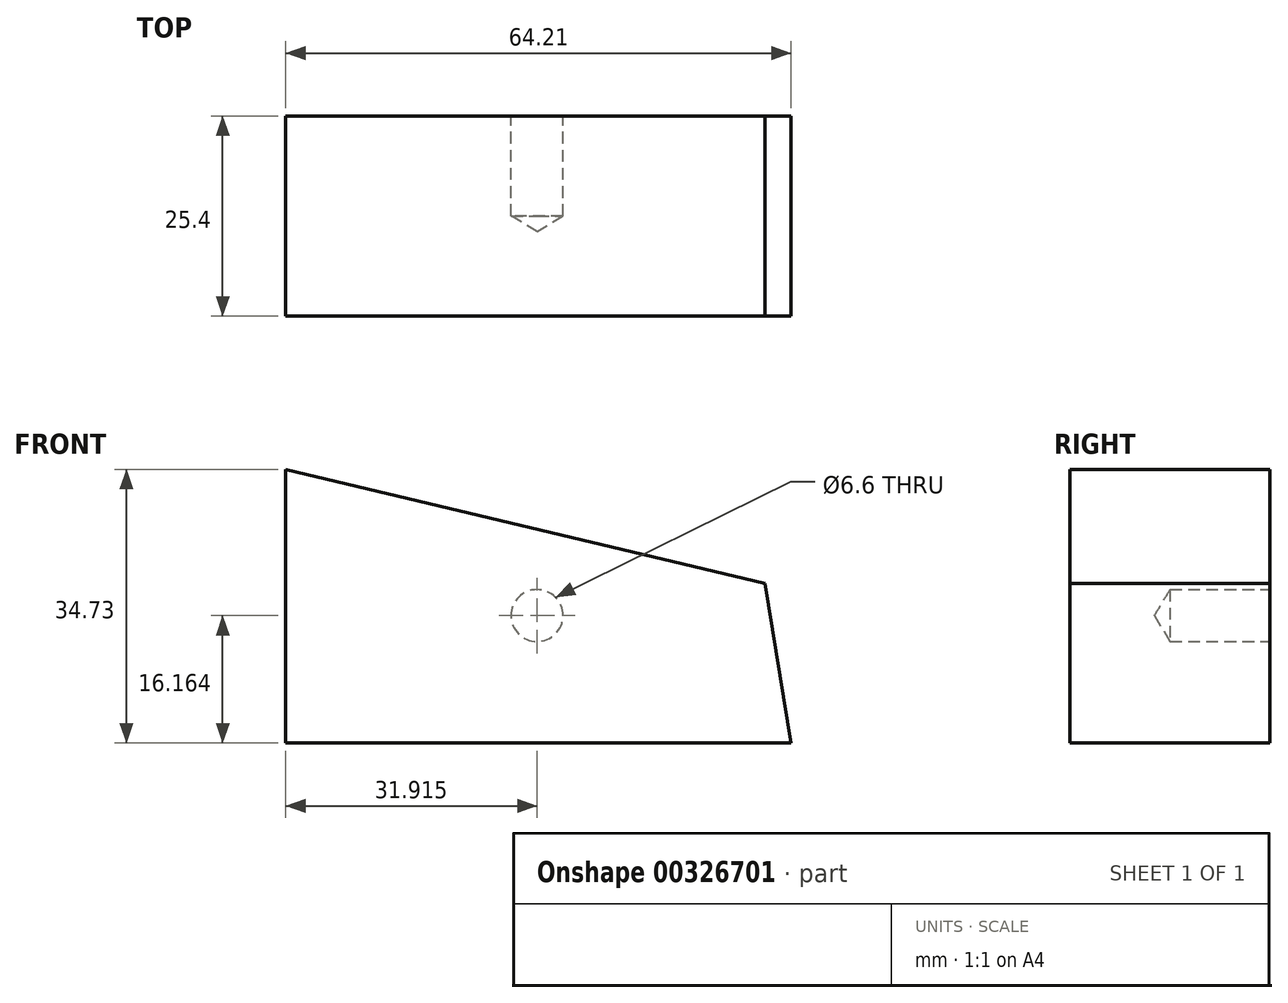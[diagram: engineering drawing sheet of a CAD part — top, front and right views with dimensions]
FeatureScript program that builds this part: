
annotation { "Feature Type Name" : "Feature", "Feature Type Description" : "" }
export const myFeature = defineFeature(function(context is Context, id is Id, definition is map)
    precondition{}
    {
        {
            var Q0;
            Q0=qCreatedBy(makeId("Front.planeOp"),FACE);
            var sketch = newSketch(context, id + "F0", { "sketchPlane" : qUnion([Q0])});
            skLineSegment(sketch, "E0", {"start": v(-64.21, 34.73) * mm, "end": v(-64.21, 0) * mm});
            skLineSegment(sketch, "E1", {"start": v(-64.21, 0) * mm, "end": v(0, 0) * mm});
            skLineSegment(sketch, "E2", {"start": v(0, 0) * mm, "end": v(-3.37, 20.26) * mm});
            skLineSegment(sketch, "E3", {"start": v(-3.37, 20.26) * mm, "end": v(-64.21, 34.73) * mm});
            skSolve(sketch);
        }
        {
            var Q0;
            Q0 = qSketchRegion(id + "F0", true);
            extrude(context, id + "F1", {"entities" : qUnion([Q0]), "depth" : 25.4 * mm});
        }
        {
            var Q0;
            Q0=makeQuery(id+"F1.opExtrude","CAP_FACE",FACE,{"disambiguationData":[OSD([sQuery(id+"F0.wireOp",EDGE,"E0"),sQuery(id+"F0.wireOp",EDGE,"E1"),sQuery(id+"F0.wireOp",EDGE,"E2"),sQuery(id+"F0.wireOp",EDGE,"E3")])],"isStart":true});
            var sketch = newSketch(context, id + "F2", { "sketchPlane" : qUnion([Q0])});
            skPoint(sketch, "E4", {"position": v(32.3, 16.16) * mm});
            skSolve(sketch);
        }
        {
            var Q0;
            Q0=sQuery(id+"F2.wireOp",VERTEX,"E4");
            var Q1;
            Q1=makeQuery(id+"F1.opExtrude","SWEPT_BODY",BODY,{"disambiguationData":[OSD([sQuery(id+"F0.wireOp",EDGE,"E0"),sQuery(id+"F0.wireOp",EDGE,"E1"),sQuery(id+"F0.wireOp",EDGE,"E2"),sQuery(id+"F0.wireOp",EDGE,"E3")])]});
            hole(context, id + "F3", {"style" : HoleStyle.SIMPLE, "endStyle" : HoleEndStyle.BLIND, "standardTappedOrClearance" : lookupTablePath({ "standard" : "ISO", "fit" : "Normal", "size" : "M6", "type" : "Clearance" }), "standardBlindInLast" : lookupTablePath({ "fit" : "Standard", "standard" : "ISO", "size" : "M6", "type" : "Clearance" }), "holeDiameter" : 6.6 * mm, "holeDepth" : 12.7 * mm, "tappedDepth" : 12.7 * mm, "tapClearance" : 3, "locations" : qUnion([Q0]), "scope" : qUnion([Q1])});
        }
    });
